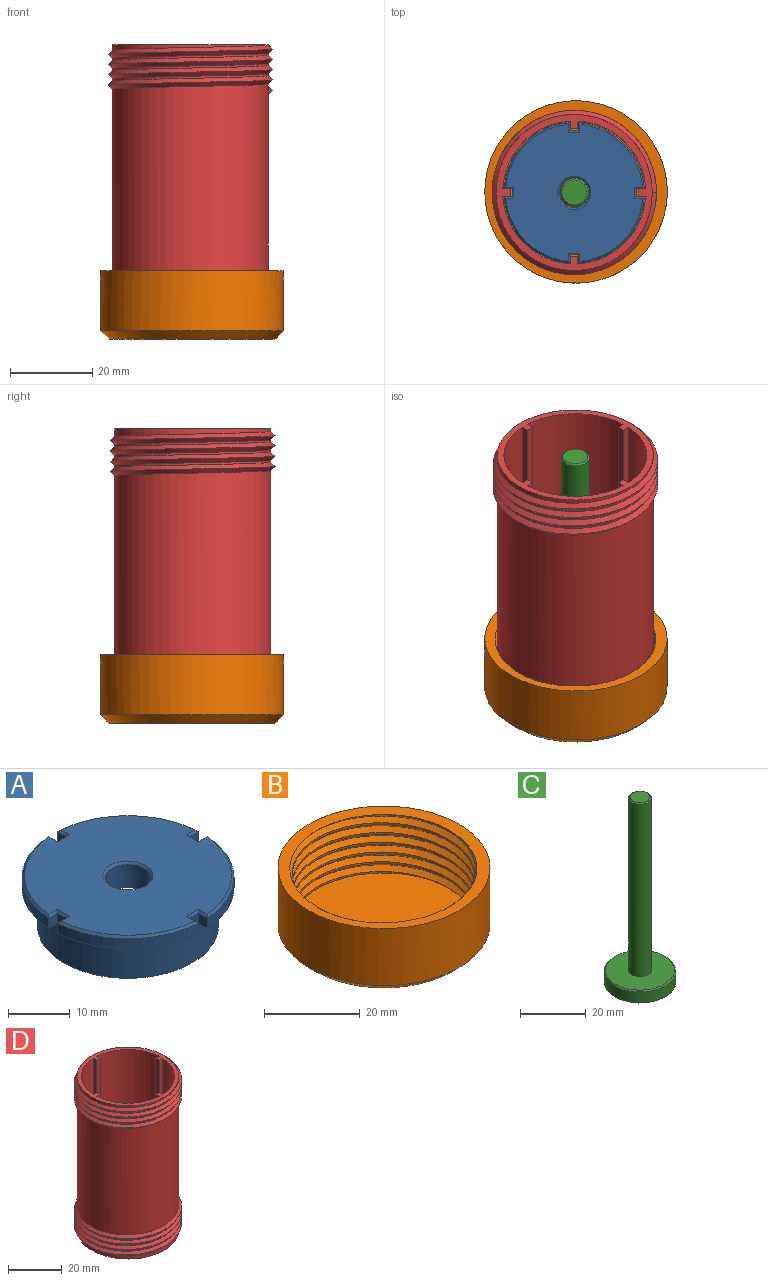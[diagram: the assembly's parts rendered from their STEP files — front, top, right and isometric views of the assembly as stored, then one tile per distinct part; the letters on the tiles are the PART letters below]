
ASSEMBLY  parts=4 mates=6
PART A: 41 faces, bbox 34.1x34.1x10 mm
  f0: cylinder r=17.1mm len=16.07mm, axis (0,0,1), area 49.7mm2, adj f11,f15,f22,f39
  f1: cylinder r=17.1mm len=16.07mm, axis (0,0,1), area 49.7mm2, adj f8,f12,f29,f39
  f2: cylinder r=17.1mm len=16.07mm, axis (0,0,1), area 49.7mm2, adj f5,f9,f37,f39
  f3: plane 29.2x29.2mm, normal (0,0,-1), area 254.3mm2, adj f21,f40
  f4: cylinder r=17.1mm len=16.07mm, axis (0,0,1), area 49.7mm2, adj f6,f14,f30,f39
  f5: plane 2x1.97mm, normal (0,1,0), area 3.9mm2, adj f2,f7,f36,f39
  f6: plane 2x1.97mm, normal (0,-1,0), area 3.9mm2, adj f4,f7,f32,f39
  f7: plane 2x2mm, normal (1,0,0), area 4mm2, adj f5,f6,f34,f39
  f8: plane 2x1.97mm, normal (1,0,0), area 3.9mm2, adj f1,f10,f31,f39
  f9: plane 2x1.97mm, normal (-1,0,0), area 3.9mm2, adj f2,f10,f35,f39
  f10: plane 2x2mm, normal (0,-1,0), area 4mm2, adj f8,f9,f33,f39
  f11: plane 2x1.97mm, normal (0,-1,0), area 3.9mm2, adj f0,f13,f23,f39
  f12: plane 2x1.97mm, normal (0,1,0), area 3.9mm2, adj f1,f13,f27,f39
  f13: plane 2x2mm, normal (-1,0,0), area 4mm2, adj f11,f12,f25,f39
  f14: plane 2x1.97mm, normal (-1,0,0), area 3.9mm2, adj f4,f16,f28,f39
  f15: plane 2x1.97mm, normal (1,0,0), area 3.9mm2, adj f0,f16,f24,f39
  f16: plane 2x2mm, normal (0,1,0), area 4mm2, adj f14,f15,f26,f39
  f17: plane 33.28x33.28mm, normal (0,0,1), area 802.4mm2, adj f22,f23,f24,f25,f26,f27,f28,f29
  f18: cylinder r=11.1mm len=22.2mm, axis (0,0,1), area 320.8mm2, adj f19,f21
  f19: plane 22.2x22.2mm, normal (0,0,-1), area 345.1mm2, adj f18,f20
  f20: cylinder r=3.65mm len=7.3mm, axis (0,0,1), area 105.5mm2, adj f19,f38
  f21: cone r=11.5mm half-angle=45deg, axis (0,0,-1), area 40.2mm2, adj f3,f18
  f22: cone r=16.7mm half-angle=45deg, axis (0,0,-1), area 13.7mm2, adj f0,f17,f23,f24
  f23: plane 2.38x0.4mm, normal (0,-0.71,0.71), area 1.1mm2, adj f11,f17,f22,f25
  f24: plane 2.38x0.4mm, normal (0.71,0,0.71), area 1.1mm2, adj f15,f17,f22,f26
  f25: plane 2.8x0.4mm, normal (-0.71,0,0.71), area 1.4mm2, adj f13,f17,f23,f27
  f26: plane 2.8x0.4mm, normal (0,0.71,0.71), area 1.4mm2, adj f16,f17,f24,f28
  f27: plane 2.38x0.4mm, normal (0,0.71,0.71), area 1.1mm2, adj f12,f17,f25,f29
  f28: plane 2.38x0.4mm, normal (-0.71,0,0.71), area 1.1mm2, adj f14,f17,f26,f30
  f29: cone r=16.7mm half-angle=45deg, axis (0,0,-1), area 13.7mm2, adj f1,f17,f27,f31
  f30: cone r=16.7mm half-angle=45deg, axis (0,0,-1), area 13.7mm2, adj f4,f17,f28,f32
  f31: plane 2.38x0.4mm, normal (0.71,0,0.71), area 1.1mm2, adj f8,f17,f29,f33
  f32: plane 2.38x0.4mm, normal (0,-0.71,0.71), area 1.1mm2, adj f6,f17,f30,f34
  f33: plane 2.8x0.4mm, normal (0,-0.71,0.71), area 1.4mm2, adj f10,f17,f31,f35
  f34: plane 2.8x0.4mm, normal (0.71,0,0.71), area 1.4mm2, adj f7,f17,f32,f36
  f35: plane 2.38x0.4mm, normal (-0.71,0,0.71), area 1.1mm2, adj f9,f17,f33,f37
  f36: plane 2.38x0.4mm, normal (0,0.71,0.71), area 1.1mm2, adj f5,f17,f34,f37
  f37: cone r=16.7mm half-angle=45deg, axis (0,0,-1), area 13.7mm2, adj f2,f17,f35,f36
  f38: cone r=3.65mm half-angle=45deg, axis (0,0,1), area 13.7mm2, adj f17,f20
  f39: plane 34.14x34.14mm, normal (0,0,-1), area 233mm2, adj f0,f1,f2,f4,f5,f6,f7,f8
  f40: cylinder r=14.6mm len=29.2mm, axis (0,0,-1), area 697.2mm2, adj f3,f39
PART B: 8 faces, bbox 45.2x47.4x18.6 mm
  f0: bspline ~46.68x40.42mm, area 1064.2mm2, adj f1,f2,f3,f4
  f1: bspline ~46.68x40.42mm, area 1063.9mm2, adj f0,f2,f3,f4
  f2: cylinder r=19.2mm len=38.4mm, axis (0,0,-1), area 334.7mm2, adj f0,f1,f3,f4
  f3: plane 39.98x39.94mm, normal (0,0,1), area 1208.3mm2, adj f0,f1,f2
  f4: plane 45.15x45.15mm, normal (0,0,1), area 339.9mm2, adj f0,f1,f2,f5
  f5: cylinder r=22.2mm len=44.4mm, axis (0,0,-1), area 2036.5mm2, adj f4,f7
  f6: plane 40.4x40.4mm, normal (0,0,-1), area 1281.9mm2, adj f7
  f7: cone r=20.2mm half-angle=45deg, axis (0,0,1), area 376.8mm2, adj f5,f6
PART C: 8 faces, bbox 21.8x21.8x69.4 mm
  f0: cylinder r=10.9mm len=21.8mm, axis (0,0,1), area 273.9mm2, adj f6,f7
  f1: plane 21x21mm, normal (0,0,-1), area 346.3mm2, adj f7
  f2: plane 6.1x6.1mm, normal (0,0,1), area 29.2mm2, adj f5
  f3: cylinder r=3.45mm len=64.19mm, axis (0,0,1), area 1391.5mm2, adj f4,f5
  f4: plane 21x21mm, normal (0,0,1), area 308.9mm2, adj f3,f6
  f5: cone r=3.05mm half-angle=45deg, axis (0,0,-1), area 11.6mm2, adj f2,f3
  f6: cone r=10.5mm half-angle=45deg, axis (0,0,-1), area 38mm2, adj f0,f4
  f7: cone r=10.9mm half-angle=45deg, axis (0,0,1), area 38mm2, adj f0,f1
PART D: 35 faces, bbox 40x46.2x70 mm
  f0: cylinder r=19mm len=38mm, axis (0,0,1), area 59.7mm2, adj f1,f4,f29,f30
  f1: cylinder r=19mm len=38mm, axis (0,0,1), area 59.7mm2, adj f0,f2,f29,f30
  f2: cylinder r=19mm len=38mm, axis (0,0,1), area 59.7mm2, adj f1,f3,f29,f30
  f3: cylinder r=19mm len=38mm, axis (0,0,1), area 149.2mm2, adj f2,f26,f27,f29
  f4: cylinder r=19mm len=51mm, axis (0,0,1), area 5790mm2, adj f0,f5,f28,f30,f32,f33
  f5: cylinder r=19mm len=38mm, axis (0,0,1), area 59.7mm2, adj f4,f6,f33,f34
  f6: cylinder r=19mm len=38mm, axis (0,0,1), area 59.7mm2, adj f5,f7,f33,f34
  f7: cylinder r=19mm len=38mm, axis (0,0,1), area 59.7mm2, adj f6,f8,f33,f34
  f8: cylinder r=19mm len=38mm, axis (0,0,1), area 149.2mm2, adj f7,f25,f31,f34
  f9: plane 70x1.78mm, normal (1,0,0), area 124.4mm2, adj f10,f24,f25,f26
  f10: cylinder r=17.4mm len=70mm, axis (0,0,1), area 1787.2mm2, adj f9,f11,f25,f26
  f11: plane 70x1.78mm, normal (0,1,0), area 124.4mm2, adj f10,f12,f25,f26
  f12: plane 70x1.8mm, normal (-1,0,0), area 126mm2, adj f11,f13,f25,f26
  f13: plane 70x1.78mm, normal (0,-1,0), area 124.4mm2, adj f12,f14,f25,f26
  f14: cylinder r=17.4mm len=70mm, axis (0,0,1), area 1787.2mm2, adj f13,f15,f25,f26
  f15: plane 70x1.78mm, normal (1,0,0), area 124.4mm2, adj f14,f16,f25,f26
  f16: plane 70x1.8mm, normal (0,1,0), area 126mm2, adj f15,f17,f25,f26
  f17: plane 70x1.78mm, normal (-1,0,0), area 124.4mm2, adj f16,f18,f25,f26
  f18: cylinder r=17.4mm len=70mm, axis (0,0,1), area 1787.2mm2, adj f17,f19,f25,f26
  f19: plane 70x1.78mm, normal (0,-1,0), area 124.4mm2, adj f18,f20,f25,f26
  f20: plane 70x1.8mm, normal (1,0,0), area 126mm2, adj f19,f21,f25,f26
  f21: plane 70x1.78mm, normal (0,1,0), area 124.4mm2, adj f20,f22,f25,f26
  f22: cylinder r=17.4mm len=70mm, axis (0,0,1), area 1787.2mm2, adj f21,f23,f25,f26
  f23: plane 70x1.78mm, normal (-1,0,0), area 124.4mm2, adj f22,f24,f25,f26
  f24: plane 70x1.8mm, normal (0,-1,0), area 126mm2, adj f9,f23,f25,f26
  f25: plane 38x38mm, normal (0,0,-1), area 195.9mm2, adj f8,f9,f10,f11,f12,f13,f14,f15
  f26: plane 38x38mm, normal (0,0,1), area 195.9mm2, adj f3,f9,f10,f11,f12,f13,f14,f15
  f27: plane 2x1mm, normal (0,1,0), area 1mm2, adj f3,f29,f30
  f28: plane 2x1mm, normal (0,-1,0), area 1mm2, adj f4,f29,f30
  f29: bspline ~46.19x40mm, area 693.1mm2, adj f0,f1,f2,f3,f27,f28,f30
  f30: bspline ~46.19x40mm, area 693.7mm2, adj f0,f1,f2,f4,f27,f28,f29
  f31: plane 2x1mm, normal (0,-1,0), area 1mm2, adj f8,f33,f34
  f32: plane 2x1mm, normal (0,1,0), area 1mm2, adj f4,f33,f34
  f33: bspline ~46.19x40mm, area 693.7mm2, adj f4,f5,f6,f7,f31,f32,f34
  f34: bspline ~46.19x40mm, area 693.1mm2, adj f5,f6,f7,f8,f31,f32,f33
PLACE A t=(-9.04,-40.07,5.97)mm
PLACE B t=(-8.61,-39.85,6.17)mm
PLACE C t=(-9.04,-40.07,6.17)mm
PLACE D t=(-9.04,-40.07,5.97)mm
MATE cylindrical A.f0 <-> C.f0  axis (0,0,1) through (-9.04,-40.07,15.57)mm
MATE planar B.f3 <-> D.f0  axis (0,0,1) through (-9.03,-40.06,5.97)mm
MATE planar A.f0 <-> D.f0  axis (0,0,-1) through (-9.04,-40.07,5.97)mm
MATE planar A.f0 <-> C.f0  axis (0,0,-1) through (-9.04,-40.07,10.97)mm
MATE parallel A.f5 <-> D.f11  axis (0,1,0) through (7.04,-41.07,14.57)mm
MATE cylindrical D.f0 <-> C.f0  axis (0,0,1) through (-9.04,-40.07,40.97)mm
